FCSTD DOCUMENT  (FreeCAD 0.19R24366 (Git))
Label: MagnetResin_Assembly
License: All rights reserved
LicenseURL: http://en.wikipedia.org/wiki/All_rights_reserved
objects: App::Link×2, App::Part×1, Spreadsheet::Sheet×1
EXTERNAL_REF file=Rotor_ResinCast.FCStd obj=PocketBody
EXTERNAL_REF file=Rotor_Magnets.FCStd obj=Array
EXTERNAL_REF file=../../Master_of_Puppets.FCStd obj=Spreadsheet

FEATURE [App::Link] Link001  label="Rotor_ResinCast"
  LinkPlacement = pos=(3.6e-15,0,0) rot=(0,0,1;0rad)
  LinkedObject = -> <external Rotor_ResinCast.FCStd>#PocketBody
  Placement = pos=(3.6e-15,0,0) rot=(0,0,1;0rad)
FEATURE [App::Link] Link002  label="Rotor_Magnets"
  LinkPlacement = pos=(3.6e-15,0,10) rot=(0,0,1;0rad)
  LinkedObject = -> <external Rotor_Magnets.FCStd>#Array
  Placement = pos=(3.6e-15,0,10) rot=(0,0,1;0rad)
  expr: .Placement.Base.z = Spreadsheet.MagnetAssemblyZ
FEATURE [App::Part] Part  label="MagnetResin_Assembly"
  Group = -> [Link001,Link002]
  Origin = -> Origin
  Placement = pos=(0,0,0) rot=(0,1,0;3.14159rad)
FEATURE [Spreadsheet::Sheet] Spreadsheet
  cells = A1=Inputs; A2=RotorDiskThickness; B2(RotorDiskThickness)==Master_of_Puppets#Spreadsheet.RotorDiskThickness; A3=Magnet Assembly; A4=MagnetAssemblyZ; B4(MagnetAssemblyZ)==RotorDiskThickness

RESOLVED EXTERNAL PARTS (link-assembly join: the EXTERNAL_REF files above that resolve inside this repo's crawl, each included once):
---- part ../../Master_of_Puppets.FCStd = doc fcstd_6404554055c4 (61625 chars; too large to inline — full recipe in that document) ----
---- part Rotor_Magnets.FCStd = doc fcstd_047787b4cc6b ----
FCSTD DOCUMENT  (FreeCAD 0.20R29177 (Git))
Label: Rotor_Magnets
License: All rights reserved
LicenseURL: http://en.wikipedia.org/wiki/All_rights_reserved
objects: App::Link×1, Spreadsheet::Sheet×1, Part::FeaturePython×1
EXTERNAL_REF file=Rotor_Magnet.FCStd obj=Box
EXTERNAL_REF file=../../Master_of_Puppets.FCStd obj=Alternator
EXTERNAL_REF file=../../Master_of_Puppets.FCStd obj=Spreadsheet

FEATURE [App::Link] Link  label="Magnet"
  LinkPlacement = pos=(-25,97.902,0) rot=(0,0,1;0rad)
  LinkedObject = -> <external Rotor_Magnet.FCStd>#Box
  Placement = pos=(-25,97.902,0) rot=(0,0,1;0rad)
  expr: .Placement.Base.x = Spreadsheet.MagnetX
  expr: .Placement.Base.y = Spreadsheet.MagnetY
FEATURE [Spreadsheet::Sheet] Spreadsheet
  cells = A1=Inputs; A2=MagnetWidth; B2(MagnetWidth)==Master_of_Puppets#Spreadsheet.MagnetWidth; A3=MagnetLength; B3(MagnetLength)==Master_of_Puppets#Spreadsheet.MagnetLength; A4=RotorDiskRadius; B4(RotorDiskRadius)==Master_of_Puppets#Spreadsheet.RotorDiskRadius; A5=NumberMagnet; B5(NumberMagnet)==Master_of_Puppets#Spreadsheet.NumberMagnet; A6=DistanceOfMagnetFromCenter; B6(DistanceOfMagnetFromCenter)==Master_of_Puppets#Alternator.DistanceOfMagnetFromCenter; A7=Magnet; A8=MagnetX; B8(MagnetX)==-MagnetWidth / 2; A9=MagnetY; B9(MagnetY)==DistanceOfMagnetFromCenter
FEATURE [Part::FeaturePython] Array  label="Rotor_Magnets"  # Draft array (typed FeaturePython)
  AlwaysSyncPlacement = false
  Angle = 360
  ArrayType = 1
  Axis = (0,0,1)
  Base = -> Link
  Center = (0,0,0)
  Count = 12
  ExpandArray = false
  Fuse = false
  IntervalAxis = (0,0,0)
  IntervalX = (50,0,0)
  IntervalY = (0,50,0)
  IntervalZ = (0,0,50)
  NumberCircles = 3
  NumberPolar = 12
  NumberX = 2
  NumberY = 2
  NumberZ = 1
  Placement = pos=(3.6e-15,0,0) rot=(0,0,1;0rad)
  PlacementList = 12 placements: [(-25,97.902,0),(-70.6016,72.2856,0),(-97.2856,27.3004,0),(-97.902,-25,0),(-72.2856,-70.6016,0),(-27.3004,-97.2856,0),(25,-97.902,0),(70.6016,-72.2856,0),(97.2856,-27.3004,0),(97.902,25,0),(72.2856,70.6016,0),(27.3004,97.2856,0)]
  RadialDistance = 50
  ScaleList = (12) [(1,1,1),(1,1,1),(1,1,1),(1,1,1),(1,1,1),(1,1,1),(1,1,1),(1,1,1),(1,1,1),(1,1,1),(1,1,1),(1,1,1)]
  Symmetry = 1
  TangentialDistance = 25
  expr: NumberPolar = Spreadsheet.NumberMagnet
---- part Rotor_ResinCast.FCStd = doc fcstd_0111194ab2d2 ----
FCSTD DOCUMENT  (FreeCAD 0.20R29177 (Git))
Label: Rotor_ResinCast
License: All rights reserved
LicenseURL: http://en.wikipedia.org/wiki/All_rights_reserved
objects: Sketcher::SketchObject×2, Spreadsheet::Sheet×1, PartDesign::Pad×1, PartDesign::Pocket×1, PartDesign::Body×1
note: 7 computed .brp shape members not serialized (recipe doc carries the construction recipe); baked Part::Feature solids carry a one-line shape summary decoded from their .brp
EXTERNAL_REF file=../../Master_of_Puppets.FCStd obj=Alternator
EXTERNAL_REF file=../../Master_of_Puppets.FCStd obj=Hub
EXTERNAL_REF file=../../Master_of_Puppets.FCStd obj=Spreadsheet

FEATURE [Sketcher::SketchObject] Sketch
  FullyConstrained = true
  MapMode = 5
  Support = -> [XY_Plane001]
  expr: Constraints[2] = Spreadsheet.RotorMoldSurroundRadius
  expr: Constraints[3] = Spreadsheet.IslandRadius
  sketch-geometry (2):
    g0: Circle CenterX=0 CenterY=0 CenterZ=0 NormalX=0 NormalY=0 NormalZ=1 AngleXU=0 Radius=155
    g1: Circle CenterX=0 CenterY=0 CenterZ=0 NormalX=0 NormalY=0 NormalZ=1 AngleXU=0 Radius=77
  constraints (4):
    c: Coincident(g0,g-1)
    c: Coincident(g1,g-1)
    c: Radius(g0) = 155
    c: Radius(g1) = 77
FEATURE [Spreadsheet::Sheet] Spreadsheet
  cells = A1=Inputs; A2=RotorDiskRadius; B2(RotorDiskRadius)==Master_of_Puppets#Spreadsheet.RotorDiskRadius; A3=RotorDiskThickness; B3(RotorDiskThickness)==Master_of_Puppets#Spreadsheet.RotorDiskThickness; A4=MagnetThickness; B4(MagnetThickness)==Master_of_Puppets#Spreadsheet.MagnetThickness; A5=HubPitchCircleRadius; B5(HubPitchCircleRadius)==Master_of_Puppets#Hub.HubPitchCircleRadius; A6=MagnetLength; B6(MagnetLength)==Master_of_Puppets#Spreadsheet.MagnetLength; A7=IslandRadius; B7(IslandRadius)==Master_of_Puppets#Alternator.IslandRadius; A8=RotorMoldSurroundThickness; B8(RotorMoldSurroundThickness)==Master_of_Puppets#Alternator.RotorMoldSurroundThickness; A9=RotorMoldSurroundRadius; B9(RotorMoldSurroundRadius)==Master_of_Puppets#Alternator.RotorMoldSurroundRadius
FEATURE [PartDesign::Pad] Pad
  AllowMultiFace = false
  Direction = (0,0,1)
  Length = 20
  Length2 = 100
  Profile = -> Sketch
  Type = 0
  expr: Length = Spreadsheet.RotorMoldSurroundThickness
FEATURE [Sketcher::SketchObject] Sketch001
  FullyConstrained = true
  MapMode = 5
  Placement = pos=(0,0,0) rot=(1,0,0;3.14159rad)
  Support = -> [Pad]
  expr: Constraints[1] = Spreadsheet.RotorDiskRadius
  sketch-geometry (1):
    g0: Circle CenterX=0 CenterY=0 CenterZ=0 NormalX=0 NormalY=0 NormalZ=1 AngleXU=0 Radius=150
  constraints (2):
    c: Coincident(g0,g-1)
    c: Radius(g0) = 150
FEATURE [PartDesign::Pocket] Pocket
  AllowMultiFace = false
  BaseFeature = -> Pad
  Direction = (0,0,1)
  Length = 10
  Length2 = 100
  Profile = -> Sketch001
  Type = 0
  expr: Length = Spreadsheet.RotorDiskThickness
FEATURE [PartDesign::Body] PocketBody  label="Rotor_ResinCast"
  Group = -> [Sketch,Pad,Sketch001,Pocket]
  Origin = -> Origin001
  Placement = pos=(4e-15,0,0) rot=(0,0,1;0rad)
  Tip = -> Pocket
